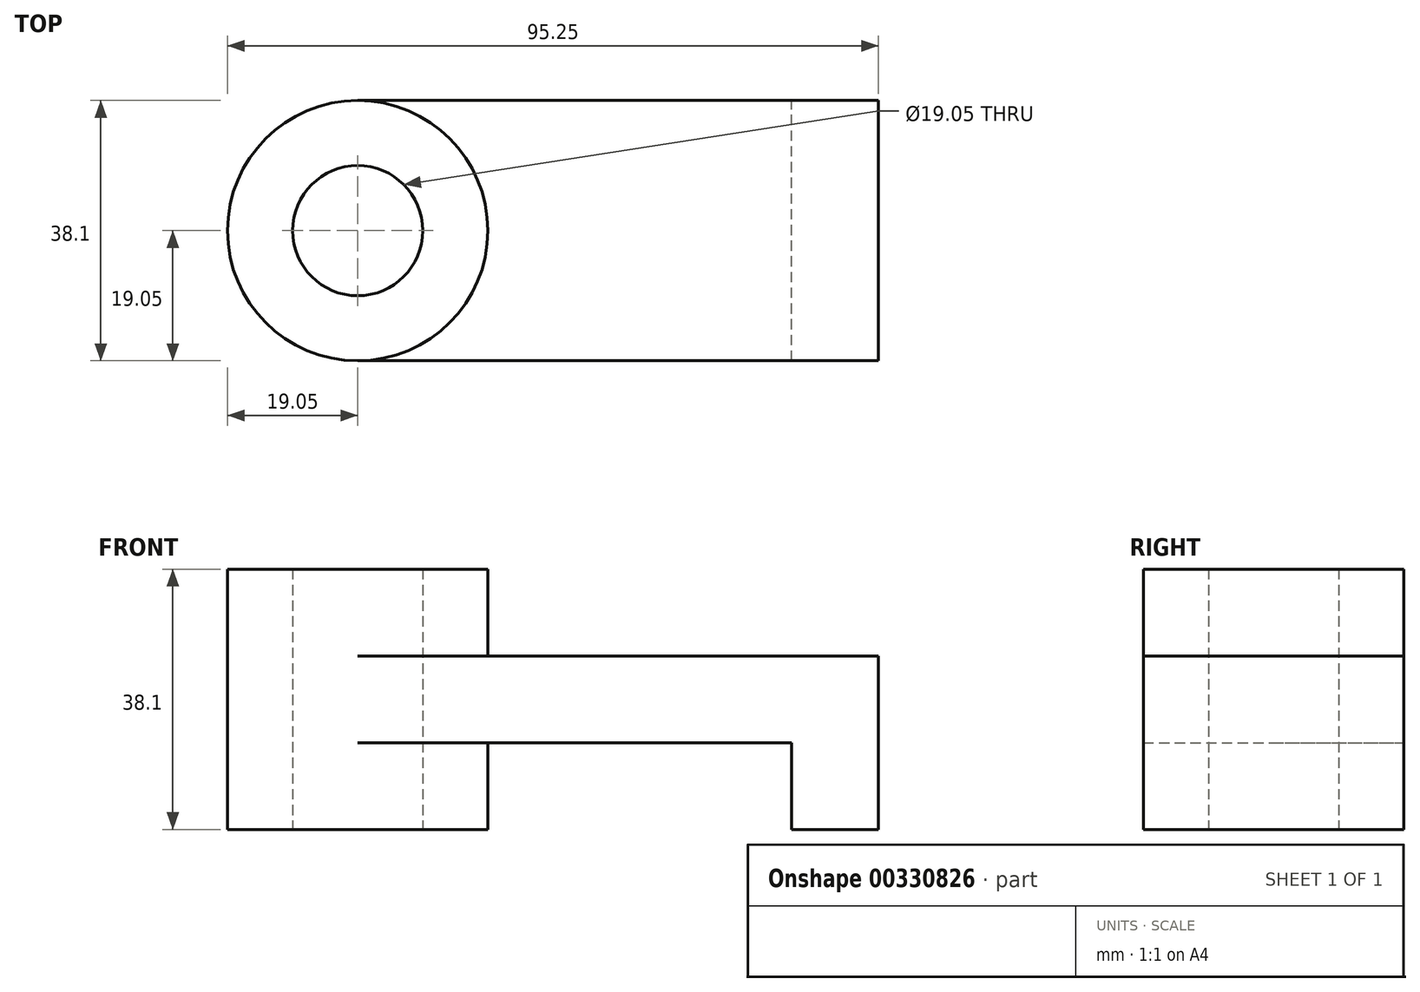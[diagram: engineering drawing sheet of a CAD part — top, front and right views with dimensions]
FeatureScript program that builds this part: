
annotation { "Feature Type Name" : "Feature", "Feature Type Description" : "" }
export const myFeature = defineFeature(function(context is Context, id is Id, definition is map)
    precondition{}
    {
        {
            var Q0;
            Q0=qCreatedBy(makeId("Top.planeOp"),FACE);
            var sketch = newSketch(context, id + "F0", { "sketchPlane" : qUnion([Q0])});
            skLineSegment(sketch, "E0.bottom", {"start": v(38.1, -19.05) * mm, "end": v(-38.1, -19.05) * mm});
            skLineSegment(sketch, "E0.top", {"start": v(38.1, 19.05) * mm, "end": v(-38.1, 19.05) * mm});
            skLineSegment(sketch, "E0.left", {"start": v(38.1, -19.05) * mm, "end": v(38.1, 19.05) * mm});
            skPoint(sketch, "E0.middle", {"position": v(0, 0) * mm});
            skCircle(sketch, "E1", {"center": v(-38.1, 0) * mm, "radius": 19.05 * mm});
            skCircle(sketch, "E2", {"center": v(-38.1, 0) * mm, "radius": 9.53 * mm});
            skSolve(sketch);
        }
        {
            var Q0;
            Q0=makeQuery(id+"F0.imprint","IMPRINT",FACE,{"disambiguationData":[TD([[makeQuery(id+"F0.imprint","IMPRINT",EDGE,{"derivedFrom":sQuery(id+"F0.wireOp",EDGE,"E2")}),-1.0]])]});
            extrude(context, id + "F1", {"entities" : qUnion([Q0]), "endBound" : BoundingType.SYMMETRIC, "depth" : 38.1 * mm});
        }
        {
            var Q0;
            {var subQ0=sQuery(id+"F0.wireOp",EDGE,"E0.bottom");Q0=makeQuery(id+"F0.imprint","IMPRINT",FACE,{"disambiguationData":[TD([[makeQuery(id+"F0.imprint","IMPRINT",EDGE,{"derivedFrom":subQ0}),-1.0]])]});}
            extrude(context, id + "F2", {"entities" : qUnion([Q0]), "operationType" : NewBodyOperationType.ADD, "endBound" : BoundingType.SYMMETRIC, "depth" : 12.7 * mm});
        }
        {
            var Q0;
            Q0=makeQuery(id+"F2.opExtrude","CAP_FACE",FACE,{"disambiguationData":[OSD([sQuery(id+"F0.wireOp",EDGE,"E0.bottom"),sQuery(id+"F0.wireOp",EDGE,"E0.top"),sQuery(id+"F0.wireOp",EDGE,"E0.left"),sQuery(id+"F0.wireOp",EDGE,"E1")])],"isStart":true});
            var sketch = newSketch(context, id + "F3", { "sketchPlane" : qUnion([Q0])});
            skLineSegment(sketch, "E3.bottom", {"start": v(38.1, 19.05) * mm, "end": v(25.4, 19.05) * mm});
            skLineSegment(sketch, "E3.top", {"start": v(38.1, -19.05) * mm, "end": v(25.4, -19.05) * mm});
            skLineSegment(sketch, "E3.left", {"start": v(38.1, 19.05) * mm, "end": v(38.1, -19.05) * mm});
            skLineSegment(sketch, "E3.right", {"start": v(25.4, 19.05) * mm, "end": v(25.4, -19.05) * mm});
            skSolve(sketch);
        }
        {
            var Q0;
            Q0=makeQuery(id+"F3.imprint","IMPRINT",FACE,{"disambiguationData":[TD([[makeQuery(id+"F3.imprint","IMPRINT",EDGE,{"derivedFrom":sQuery(id+"F3.wireOp",EDGE,"E3.bottom")}),1.0]])]});
            extrude(context, id + "F4", {"entities" : qUnion([Q0]), "operationType" : NewBodyOperationType.ADD, "depth" : 12.7 * mm});
        }
    });
